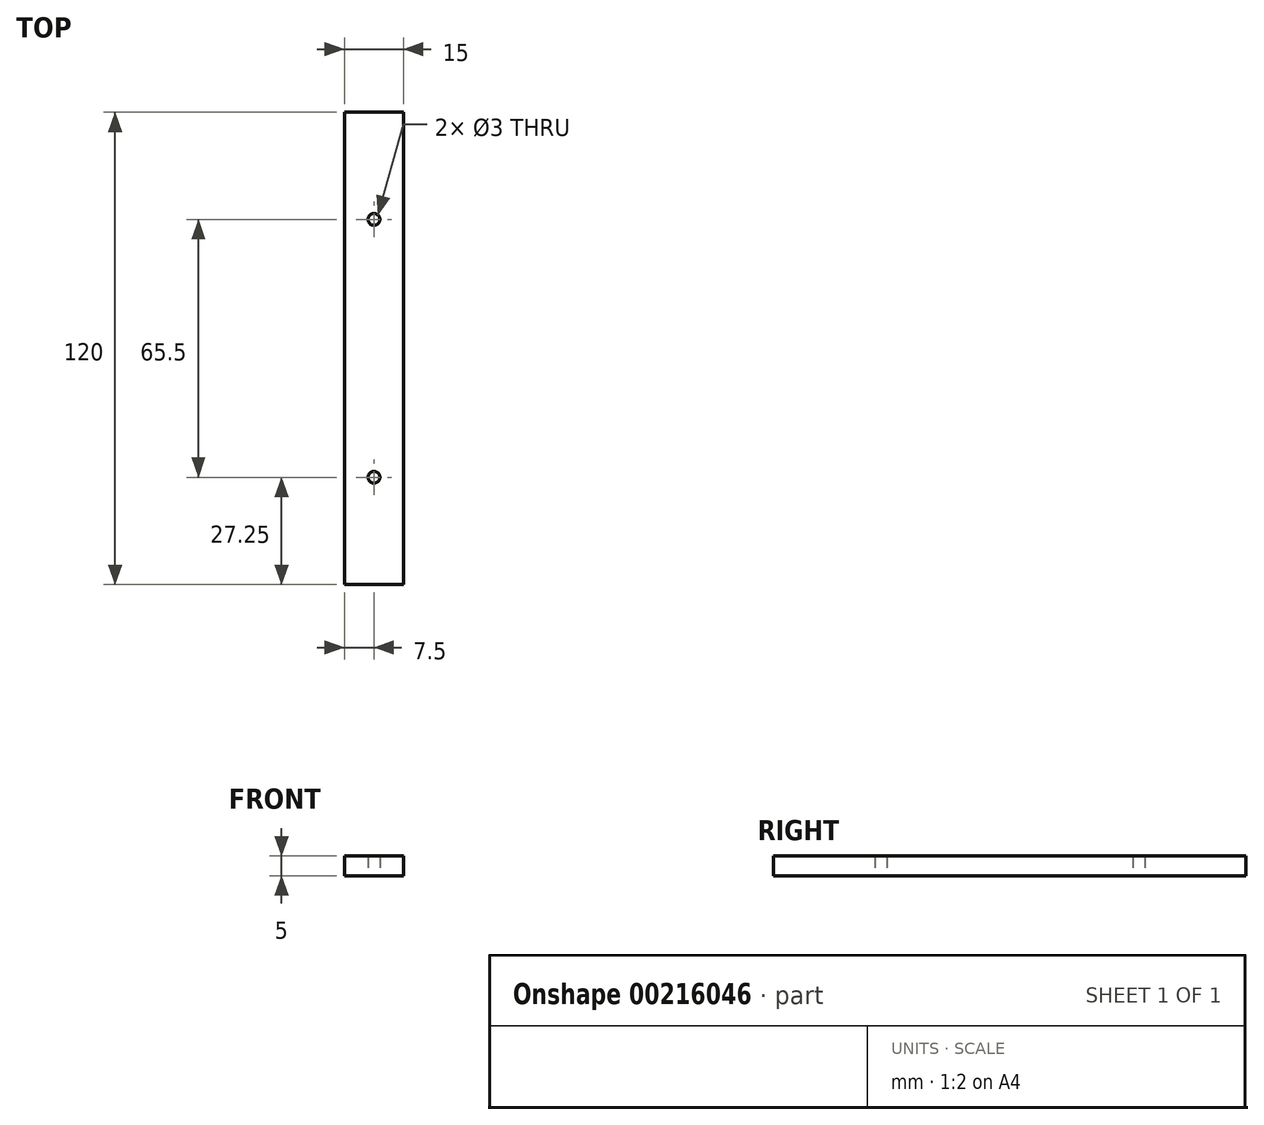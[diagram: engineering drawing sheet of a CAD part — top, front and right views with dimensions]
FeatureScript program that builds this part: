
annotation { "Feature Type Name" : "Feature", "Feature Type Description" : "" }
export const myFeature = defineFeature(function(context is Context, id is Id, definition is map)
    precondition{}
    {
        {
            var Q0;
            Q0=qCreatedBy(makeId("Top.planeOp"),FACE);
            var sketch = newSketch(context, id + "F0", { "sketchPlane" : qUnion([Q0])});
            skLineSegment(sketch, "E0.bottom", {"start": v(7.5, -60) * mm, "end": v(-7.5, -60) * mm});
            skLineSegment(sketch, "E0.top", {"start": v(7.5, 60) * mm, "end": v(-7.5, 60) * mm});
            skLineSegment(sketch, "E0.left", {"start": v(7.5, -60) * mm, "end": v(7.5, 60) * mm});
            skLineSegment(sketch, "E0.right", {"start": v(-7.5, -60) * mm, "end": v(-7.5, 60) * mm});
            skPoint(sketch, "E0.middle", {"position": v(0, 0) * mm});
            skCircle(sketch, "E1", {"center": v(0, 32.75) * mm, "radius": 1.5 * mm});
            skCircle(sketch, "E2", {"center": v(0, -32.75) * mm, "radius": 1.5 * mm});
            skLineSegment(sketch, "E3", {"start": v(0, 32.75) * mm, "end": v(0, 60) * mm, "construction": true});
            skLineSegment(sketch, "E4", {"start": v(0, -32.75) * mm, "end": v(0, -60) * mm, "construction": true});
            skSolve(sketch);
        }
        {
            var Q0;
            Q0 = qSketchRegion(id + "F0", true);
            extrude(context, id + "F1", {"entities" : qUnion([Q0]), "depth" : 5 * mm, "offsetDistance" : 25 * mm});
        }
    });
